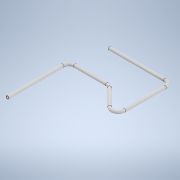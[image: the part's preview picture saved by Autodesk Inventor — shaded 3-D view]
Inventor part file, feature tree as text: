
AUTODESK INVENTOR PART (.ipt)
format: ipt  version: 2021 (Build 250183000, 183)  size: 155,648 bytes
history: native  units: mm
features: other x2, sketch x2, sweep x1
ambient origin geometry x8: Origin, YZ Plane, XZ Plane, XY Plane, X Axis, Y Axis, Z Axis, Center Point
bodies: Body1 (feature_tree)
feature tree (5):
  other  "Sólido1"
  sketch  "Esboço 3D1"  dims[d0=30.0mm d1=30.0mm]
  other  "Plano de trabalho1"
  sweep  "Varredura1"
  sketch  "Esboço1"  dims[d2=20.0mm d3=20.0mm d4=30.0mm d5=3.0mm d6=3.0mm d7=3.0mm d8=3.0mm d9=1.0mm d10=1.5mm d11=0.0mm d12=0.0mm]
